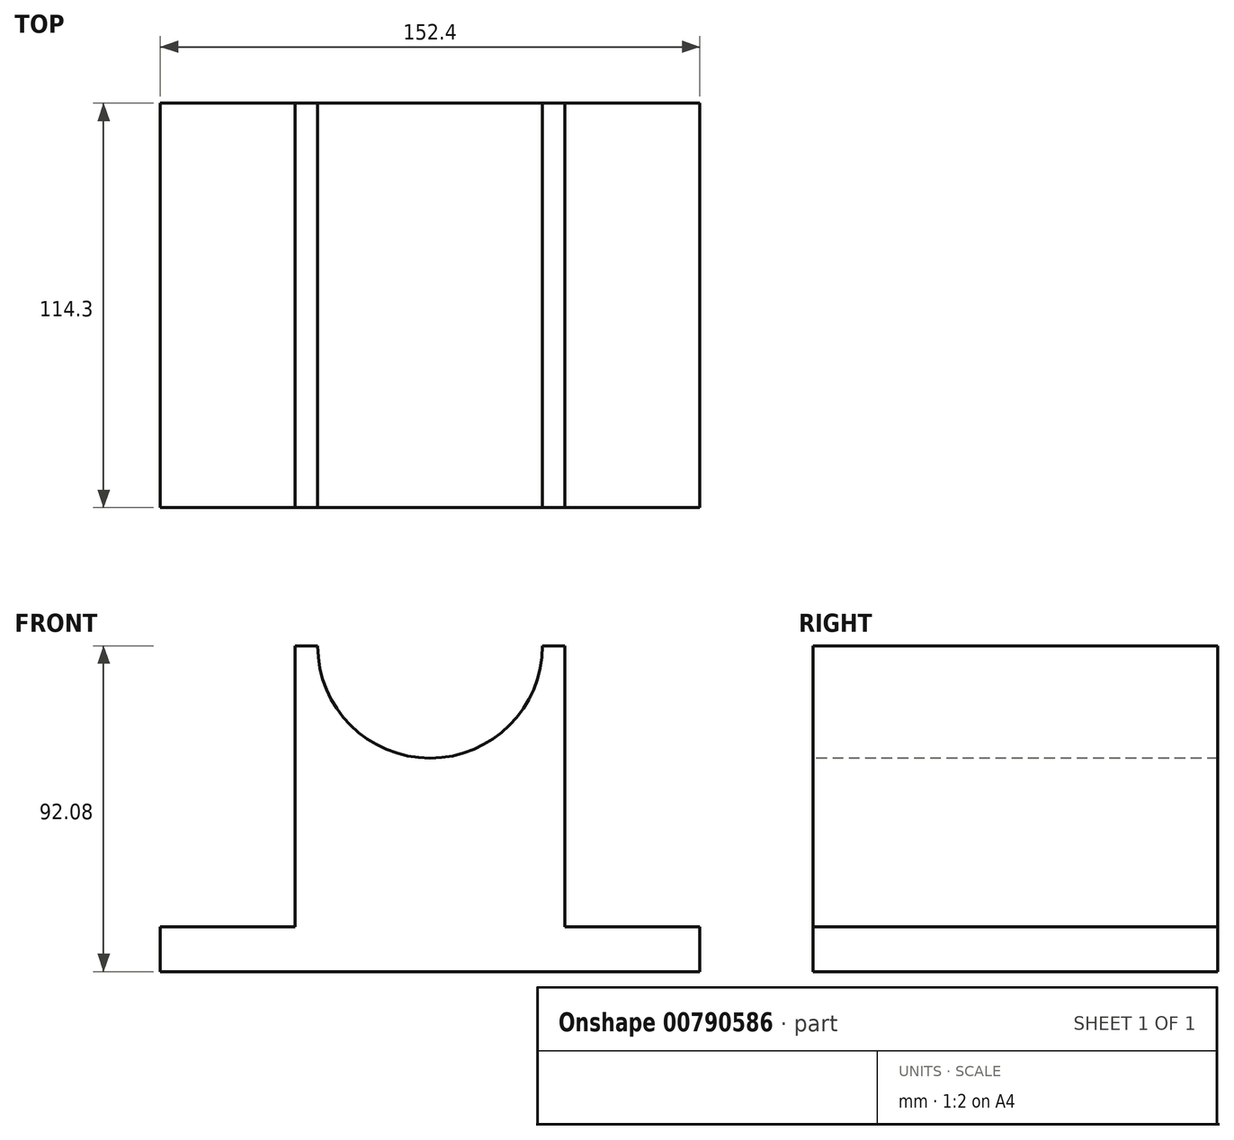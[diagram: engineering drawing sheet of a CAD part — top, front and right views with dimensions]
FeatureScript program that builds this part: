
annotation { "Feature Type Name" : "Feature", "Feature Type Description" : "" }
export const myFeature = defineFeature(function(context is Context, id is Id, definition is map)
    precondition{}
    {
        {
            var Q0;
            Q0=qCreatedBy(makeId("Front.planeOp"),FACE);
            var sketch = newSketch(context, id + "F0", { "sketchPlane" : qUnion([Q0])});
            skLineSegment(sketch, "E0", {"start": v(0, 0) * mm, "end": v(-152.4, 0) * mm});
            skLineSegment(sketch, "E1", {"start": v(-152.4, 0) * mm, "end": v(-152.4, 12.7) * mm});
            skLineSegment(sketch, "E2", {"start": v(-152.4, 12.7) * mm, "end": v(-114.3, 12.7) * mm});
            skLineSegment(sketch, "E3", {"start": v(-114.3, 12.7) * mm, "end": v(-114.3, 92.08) * mm});
            skLineSegment(sketch, "E4", {"start": v(-114.3, 92.08) * mm, "end": v(-38.1, 92.08) * mm});
            skLineSegment(sketch, "E5", {"start": v(-38.1, 92.08) * mm, "end": v(-38.1, 12.7) * mm});
            skLineSegment(sketch, "E6", {"start": v(-38.1, 12.7) * mm, "end": v(0, 12.7) * mm});
            skLineSegment(sketch, "E7", {"start": v(0, 12.7) * mm, "end": v(0, 0) * mm});
            skSolve(sketch);
        }
        {
            var Q0;
            Q0 = qSketchRegion(id + "F0", true);
            extrude(context, id + "F1", {"entities" : qUnion([Q0]), "depth" : 114.3 * mm, "offsetDistance" : 25.4 * mm});
        }
        {
            var Q0;
            Q0=makeQuery(id+"F1.opExtrude","CAP_FACE",FACE,{"disambiguationData":[OSD([sQuery(id+"F0.wireOp",EDGE,"E0"),sQuery(id+"F0.wireOp",EDGE,"E1"),sQuery(id+"F0.wireOp",EDGE,"E2"),sQuery(id+"F0.wireOp",EDGE,"E3"),sQuery(id+"F0.wireOp",EDGE,"E4"),sQuery(id+"F0.wireOp",EDGE,"E5"),sQuery(id+"F0.wireOp",EDGE,"E6"),sQuery(id+"F0.wireOp",EDGE,"E7")])],"isStart":false});
            var sketch = newSketch(context, id + "F2", { "sketchPlane" : qUnion([Q0])});
            skCircle(sketch, "E8", {"center": v(-76.2, 92.08) * mm, "radius": 31.75 * mm});
            skSolve(sketch);
        }
        {
            var Q0;
            Q0 = qSketchRegion(id + "F2", true);
            extrude(context, id + "F3", {"entities" : qUnion([Q0]), "operationType" : NewBodyOperationType.REMOVE, "endBound" : BoundingType.THROUGH_ALL, "oppositeDirection" : true, "depth" : 25.4 * mm, "offsetDistance" : 25.4 * mm});
        }
    });
